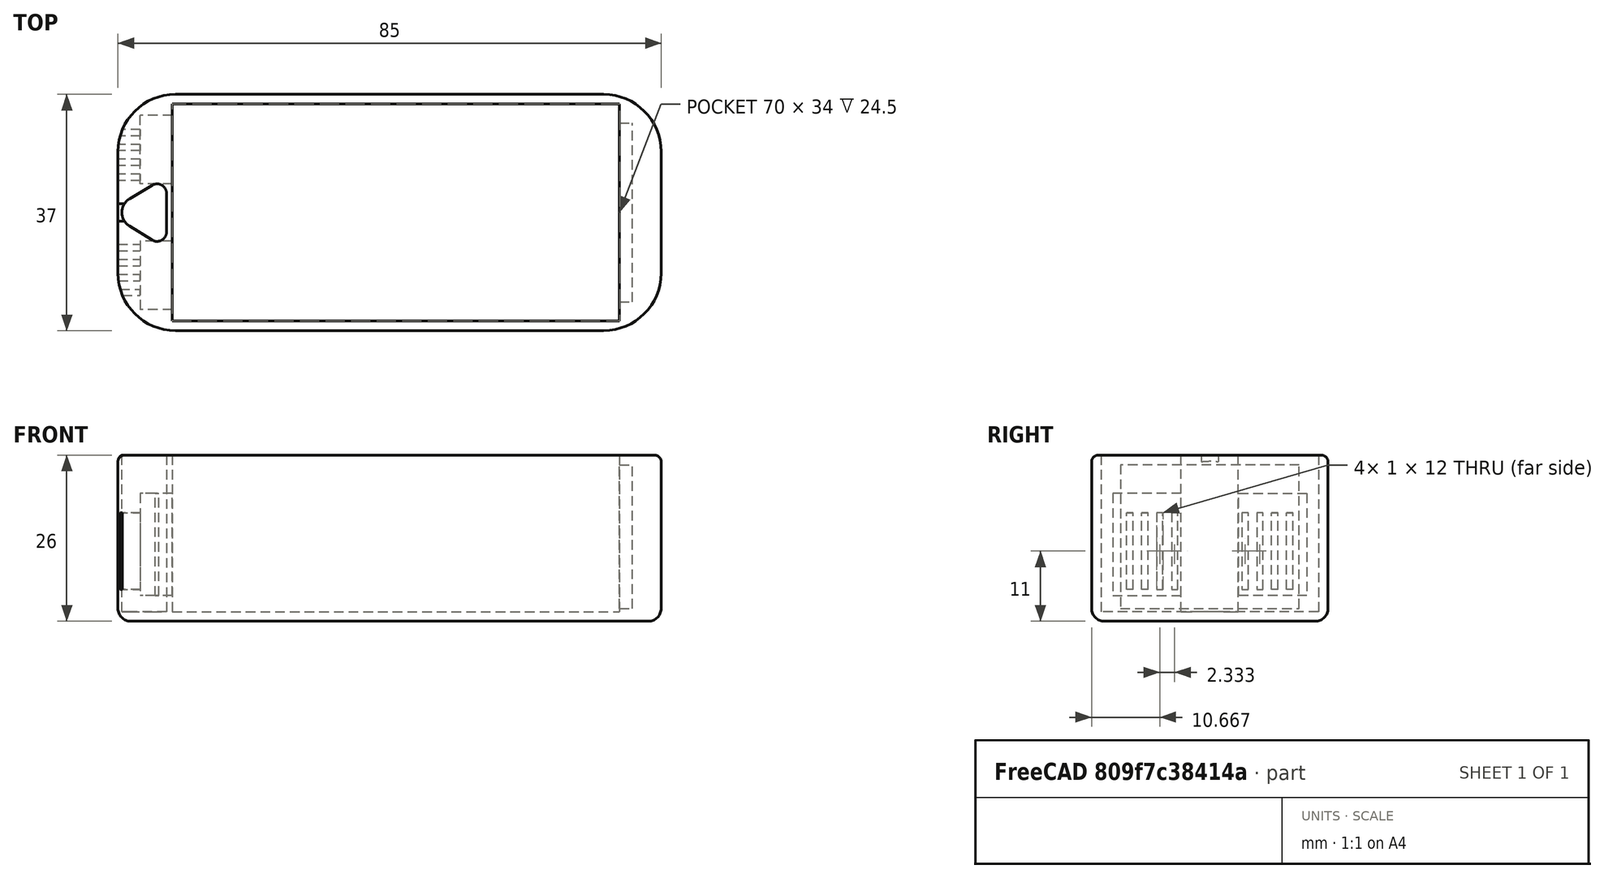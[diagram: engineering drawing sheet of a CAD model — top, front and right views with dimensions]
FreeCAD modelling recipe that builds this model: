
FCSTD DOCUMENT  (FreeCAD 0.19R24291 (Git))
Label: sensorcase
License: All rights reserved
LicenseURL: http://en.wikipedia.org/wiki/All_rights_reserved
objects: Sketcher::SketchObject×6, PartDesign::Pocket×5, PartDesign::Fillet×3, PartDesign::LinearPattern×2, PartDesign::Pad×1, PartDesign::Mirrored×1, PartDesign::Body×1, Mesh::Feature×1
note: 28 computed .brp shape members not serialized (recipe doc carries the construction recipe); baked Part::Feature solids carry a one-line shape summary decoded from their .brp

FEATURE [Sketcher::SketchObject] Sketch
  FullyConstrained = true
  MapMode = 5
  Support = -> [XY_Plane]
  sketch-geometry (4):
    g0: LineSegment StartX=-42.5 StartY=18.5 StartZ=0 EndX=42.5 EndY=18.5 EndZ=0
    g1: LineSegment StartX=42.5 StartY=18.5 StartZ=0 EndX=42.5 EndY=-18.5 EndZ=0
    g2: LineSegment StartX=42.5 StartY=-18.5 StartZ=0 EndX=-42.5 EndY=-18.5 EndZ=0
    g3: LineSegment StartX=-42.5 StartY=-18.5 StartZ=0 EndX=-42.5 EndY=18.5 EndZ=0
  constraints (11):
    c: Coincident(g0,g1)
    c: Coincident(g1,g2)
    c: Coincident(g2,g3)
    c: Coincident(g3,g0)
    c: Horizontal(g0)
    c: Horizontal(g2)
    c: Vertical(g1)
    c: Vertical(g3)
    c: DistanceX(g0,g0) = 85
    c: DistanceY(g1,g1) = 37
    c: Symmetric(g2,g0,g-1)
FEATURE [PartDesign::Pad] Pad
  Direction = (1,1,1)
  Length = 26
  Length2 = 100
  Profile = -> Sketch
  Type = 0
FEATURE [PartDesign::Fillet] Fillet
  Base = -> Pad [Edge8,Edge5,Edge2,Edge1]
  BaseFeature = -> Pad
  Radius = 9
  SupportTransform = false
FEATURE [Sketcher::SketchObject] Sketch001
  FullyConstrained = false
  MapMode = 5
  Placement = pos=(0,0,26) rot=(0,0,1;0rad)
  Support = -> [Fillet]
  sketch-geometry (10):
    g0: LineSegment StartX=-34 StartY=17 StartZ=0 EndX=36 EndY=17 EndZ=0
    g1: LineSegment StartX=36 StartY=17 StartZ=0 EndX=36 EndY=-17 EndZ=0
    g2: LineSegment StartX=36 StartY=-17 StartZ=0 EndX=-34 EndY=-17 EndZ=0
    g3: LineSegment StartX=-34 StartY=-17 StartZ=0 EndX=-34 EndY=17 EndZ=0
    g4: LineSegment StartX=-40.677 StartY=2.14243 StartZ=0 EndX=-37.1616 EndY=4.25649 EndZ=0
    g5: LineSegment StartX=-34.8885 StartY=2.97104 StartZ=0 EndX=-34.8885 EndY=-3.02896 EndZ=0
    g6: LineSegment StartX=-37.177 StartY=-4.30505 StartZ=0 EndX=-40.7026 EndY=-2.12682 EndZ=0
    g7: ArcOfCircle CenterX=-39.3885 CenterY=0 CenterZ=0 NormalX=0 NormalY=0 NormalZ=1 AngleXU=0 Radius=2.5 StartAngle=2.11223 EndAngle=4.15896
    g8: ArcOfCircle CenterX=-36.3885 CenterY=2.97104 CenterZ=0 NormalX=0 NormalY=0 NormalZ=1 AngleXU=0 Radius=1.5 StartAngle=0 EndAngle=2.11223
    g9: ArcOfCircle CenterX=-36.3885 CenterY=-3.02896 CenterZ=0 NormalX=0 NormalY=0 NormalZ=1 AngleXU=0 Radius=1.5 StartAngle=4.15896 EndAngle=6.28319
  constraints (25):
    c: Coincident(g0,g1)
    c: Coincident(g1,g2)
    c: Coincident(g2,g3)
    c: Coincident(g3,g0)
    c: Horizontal(g0)
    c: Horizontal(g2)
    c: Vertical(g1)
    c: Vertical(g3)
    c: DistanceY(g1,g1) = 34
    c: DistanceX(g0,g0) = 70
    c: DistanceY(g-1,g0) = 17
    c: DistanceX(g-1,g0) = 36
    c: Vertical(g5)
    c: Tangent(g4,g7) = 1.5708
    c: Tangent(g6,g7) = 1.5708
    c: Tangent(g4,g8) = 1.5708
    c: Tangent(g5,g8) = 1.5708
    c: Tangent(g6,g9) = 1.5708
    c: Tangent(g5,g9) = 1.5708
    c: Radius(g7) = 2.5
    c: DistanceY(g-1,g7) = 0
    c: Radius(g9) = 1.5
    c: Equal(g9,g8)
    c: DistanceX(g7,g5) = 4.5
    c: DistanceY(g5,g5) = 6
FEATURE [PartDesign::Pocket] Pocket
  BaseFeature = -> Fillet
  Length = 24.5
  Length2 = 100
  Profile = -> Sketch001
  Type = 0
FEATURE [Sketcher::SketchObject] Sketch002
  FullyConstrained = true
  MapMode = 5
  Placement = pos=(-34,0,0) rot=(0.57735,0.57735,0.57735;2.0944rad)
  Support = -> [Pocket]
  sketch-geometry (4):
    g0: LineSegment StartX=4.5 StartY=20 StartZ=0 EndX=15.2 EndY=20 EndZ=0
    g1: LineSegment StartX=15.2 StartY=20 StartZ=0 EndX=15.2 EndY=4 EndZ=0
    g2: LineSegment StartX=15.2 StartY=4 StartZ=0 EndX=4.5 EndY=4 EndZ=0
    g3: LineSegment StartX=4.5 StartY=4 StartZ=0 EndX=4.5 EndY=20 EndZ=0
  constraints (12):
    c: Coincident(g0,g1)
    c: Coincident(g1,g2)
    c: Coincident(g2,g3)
    c: Coincident(g3,g0)
    c: Horizontal(g0)
    c: Horizontal(g2)
    c: Vertical(g1)
    c: Vertical(g3)
    c: DistanceX(g0,g0) = 10.7
    c: DistanceY(g1,g1) = 16
    c: DistanceX(g-1,g0) = 4.5
    c: DistanceY(g-1,g1) = 4
FEATURE [PartDesign::Pocket] Pocket001
  BaseFeature = -> Pocket
  Length = 5
  Length2 = 100
  Profile = -> Sketch002
  Type = 0
FEATURE [Sketcher::SketchObject] Sketch003
  FullyConstrained = true
  MapMode = 5
  Placement = pos=(-39,0,0) rot=(0.57735,0.57735,0.57735;2.0944rad)
  Support = -> [Pocket001]
  sketch-geometry (4):
    g0: LineSegment StartX=5 StartY=17 StartZ=0 EndX=6 EndY=17 EndZ=0
    g1: LineSegment StartX=6 StartY=17 StartZ=0 EndX=6 EndY=5 EndZ=0
    g2: LineSegment StartX=6 StartY=5 StartZ=0 EndX=5 EndY=5 EndZ=0
    g3: LineSegment StartX=5 StartY=5 StartZ=0 EndX=5 EndY=17 EndZ=0
  constraints (12):
    c: Coincident(g0,g1)
    c: Coincident(g1,g2)
    c: Coincident(g2,g3)
    c: Coincident(g3,g0)
    c: Horizontal(g0)
    c: Horizontal(g2)
    c: Vertical(g1)
    c: Vertical(g3)
    c: DistanceX(g2,g2) = 1
    c: DistanceY(g1,g1) = 12
    c: DistanceY(g-1,g1) = 5
    c: DistanceX(g-1,g2) = 5
FEATURE [PartDesign::Pocket] Pocket002
  BaseFeature = -> Pocket001
  Length = 5
  Length2 = 100
  Profile = -> Sketch003
  Type = 1
FEATURE [PartDesign::LinearPattern] LinearPattern
  BaseFeature = -> Pocket002
  Direction = -> Y_Axis
  Length = 7
  Occurrences = 4
  Originals = -> [Pocket002]
FEATURE [Sketcher::SketchObject] Sketch004
  FullyConstrained = true
  MapMode = 5
  Placement = pos=(36,0,0) rot=(0.57735,-0.57735,-0.57735;2.0944rad)
  Support = -> [LinearPattern]
  sketch-geometry (4):
    g0: LineSegment StartX=-14 StartY=24.5 StartZ=0 EndX=14 EndY=24.5 EndZ=0
    g1: LineSegment StartX=14 StartY=24.5 StartZ=0 EndX=14 EndY=2 EndZ=0
    g2: LineSegment StartX=14 StartY=2 StartZ=0 EndX=-14 EndY=2 EndZ=0
    g3: LineSegment StartX=-14 StartY=2 StartZ=0 EndX=-14 EndY=24.5 EndZ=0
  constraints (12):
    c: Coincident(g0,g1)
    c: Coincident(g1,g2)
    c: Coincident(g2,g3)
    c: Coincident(g3,g0)
    c: Horizontal(g0)
    c: Horizontal(g2)
    c: Vertical(g1)
    c: Vertical(g3)
    c: DistanceX(g0,g0) = 28
    c: DistanceY(g-1,g1) = 2
    c: DistanceX(g-1,g0) = 14
    c: DistanceY(g1,g1) = 22.5
FEATURE [PartDesign::Pocket] Pocket003
  BaseFeature = -> LinearPattern
  Length = 2
  Length2 = 100
  Profile = -> Sketch004
  Type = 0
FEATURE [PartDesign::Mirrored] Mirrored
  BaseFeature = -> Pocket003
  MirrorPlane = -> Sketch002 [V_Axis]
  Originals = -> [Pocket001]
FEATURE [Sketcher::SketchObject] Sketch005
  FullyConstrained = true
  MapMode = 5
  Placement = pos=(-42.5,0,0) rot=(0.57735,-0.57735,-0.57735;2.0944rad)
  Support = -> [Mirrored]
  sketch-geometry (4):
    g0: LineSegment StartX=5 StartY=17 StartZ=0 EndX=6 EndY=17 EndZ=0
    g1: LineSegment StartX=6 StartY=17 StartZ=0 EndX=6 EndY=5 EndZ=0
    g2: LineSegment StartX=6 StartY=5 StartZ=0 EndX=5 EndY=5 EndZ=0
    g3: LineSegment StartX=5 StartY=5 StartZ=0 EndX=5 EndY=17 EndZ=0
  constraints (12):
    c: Coincident(g0,g1)
    c: Coincident(g1,g2)
    c: Coincident(g2,g3)
    c: Coincident(g3,g0)
    c: Horizontal(g0)
    c: Horizontal(g2)
    c: Vertical(g1)
    c: Vertical(g3)
    c: DistanceX(g0,g0) = 1
    c: DistanceY(g3,g3) = 12
    c: DistanceY(g-1,g1) = 5
    c: DistanceX(g-1,g2) = 5
FEATURE [PartDesign::Pocket] Pocket004
  BaseFeature = -> Mirrored
  Length = 18
  Length2 = 100
  Profile = -> Sketch005
  Type = 0
FEATURE [PartDesign::LinearPattern] LinearPattern001
  BaseFeature = -> Pocket004
  Direction = -> Y_Axis
  Length = 7
  Occurrences = 4
  Originals = -> [Pocket004]
  Reversed = true
FEATURE [PartDesign::Fillet] Fillet001
  Base = -> LinearPattern001 [Edge7,Edge9,Edge11,Edge10,Edge8,Edge6,Edge1,Edge5]
  BaseFeature = -> LinearPattern001
  Radius = 2
  SupportTransform = false
FEATURE [PartDesign::Fillet] Fillet002
  Base = -> Fillet001 [Edge20,Edge6,Edge3,Edge19,Edge21,Edge23,Edge24,Edge22]
  BaseFeature = -> Fillet001
  Radius = 1
  SupportTransform = false
FEATURE [PartDesign::Body] Body
  Group = -> [Sketch,Pad,Fillet,Sketch001,Pocket,Sketch002,Pocket001,Sketch003,Pocket002,LinearPattern,Sketch004,Pocket003,Mirrored,Sketch005,Pocket004,LinearPattern001,Fillet001,Fillet002]
  Origin = -> Origin
  Tip = -> Fillet002
FEATURE [Mesh::Feature] Mesh  label="Fillet002 (Meshed)"
